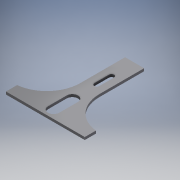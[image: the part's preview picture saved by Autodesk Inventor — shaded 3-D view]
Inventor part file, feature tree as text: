
AUTODESK INVENTOR PART (.ipt)
format: ipt  version: 2017 (Build 210142000, 142)  size: 125,952 bytes
history: native  units: mm
features: reference x15, other x4, extrude x1, sketch x1
ambient origin geometry x8: Origin, YZ Plane, XZ Plane, XY Plane, X Axis, Y Axis, Z Axis, Center Point
bodies: Solid1 (feature_tree)
feature tree (21):
  extrude  "Extrusion1"  Depth=6.0mm TaperAngle=0.0deg
  sketch  "Sketch1"  dims[d2=26.0mm d3=6.0mm d4=0.0mm d5=22.0mm]
  reference  "Reference1"
  reference  "Reference2"
  reference  "Reference3"
  reference  "Reference4"
  reference  "Reference5"
  reference  "Reference6"
  reference  "Reference7"
  reference  "Reference8"
  reference  "Reference9"
  reference  "Reference10"
  reference  "Reference11"
  reference  "Reference13"
  reference  "Reference14"
  reference  "Reference15"
  reference  "Reference16"
  other  "<userpath>\Dropbox\Work\Project\Inventor\Base Assembly.iam"
  other  "Base Assembly.iam"
  other  "Camera stand plate base:1"
  other  "Camera mounting back:1"
